# Revit family: Gira_216000
name_source: partatom
category: Electrical Fixtures
revit_build: Autodesk Revit 2017 (Build: 20160225_1515(x64)
units: mm (PartAtom-declared; Revit-internal decimal feet)

## family parameters
Cut with Voids When Loaded = No
Host = Face
Maintain Annotation Orientation = No
Part Type = Normal
Room Calculation Point = No
Round Connector Dimension = Use Diameter
Shared = No

## types (1)
- Shutter act. 4-g AC 230 V man.act. KNX DRA
    BIM = https://media.live.bim.site 8f.rfa
    BIMSITE_PRODUCT_ID = e0d490d711951edfc0e10b13a19cc258dc9395b6
    Bus connection included = Yes
    Cost = 0 $
    Default Elevation = 1219 mm
    Description = Blind act.4g AC 230V DRA KNX KNX shutter actuator, 4-gang AC 230 V with manual actuation,DRA plus Features: - Shutter actuator with manual actuation and status display for each output. - With integrated bus coupler. - For controlling electrically operated shutters for mains voltage of AC 230 V (4-channel). - Connection of various external conductors. - Independent control of the four shutter outputs. - Shutter position can be directly controlled. - Behaviour after bus voltage failure and recovery can be set. - Feedback of position. Active or passive (object can be read out) cyclical feedback functions. - Assignments of up to five different safety functions (three wind alarms, one rain alarm, one frost alarm) or optionally with cyclical monitoring. - Building site operation: Outputs can be operated manually without bus voltage with operating voltage only.,Notes : - VDE approval in accordance with EN 60669-1, EN 60669-2-1. - Installation on DIN top-hat rail.
    GTIN = 4010337101352
    HAN = 216000
    Handschaltung = No
    HeinzeBIM = https://www.heinze.de
    Local operation/hand operation = Yes
    Manufacturer = Gira
    Max. number of venetian-blind outputs = 4
    Number of binary inputs = 0
    Number of inputs = 1
    Number of outputs = 0
    Rated current [Ampere] = 0
    Stellgröße schaltend = No
    Stellgröße stetig = No
    Suitable for C-load = No
    URL = https://www.gira.de
    Ventilschutzfunktion = No
    With switch function = No

## geometry (parser evidence)
native form markers: Blend x2, Sweep x3
no freeform markers — native parametric forms only
